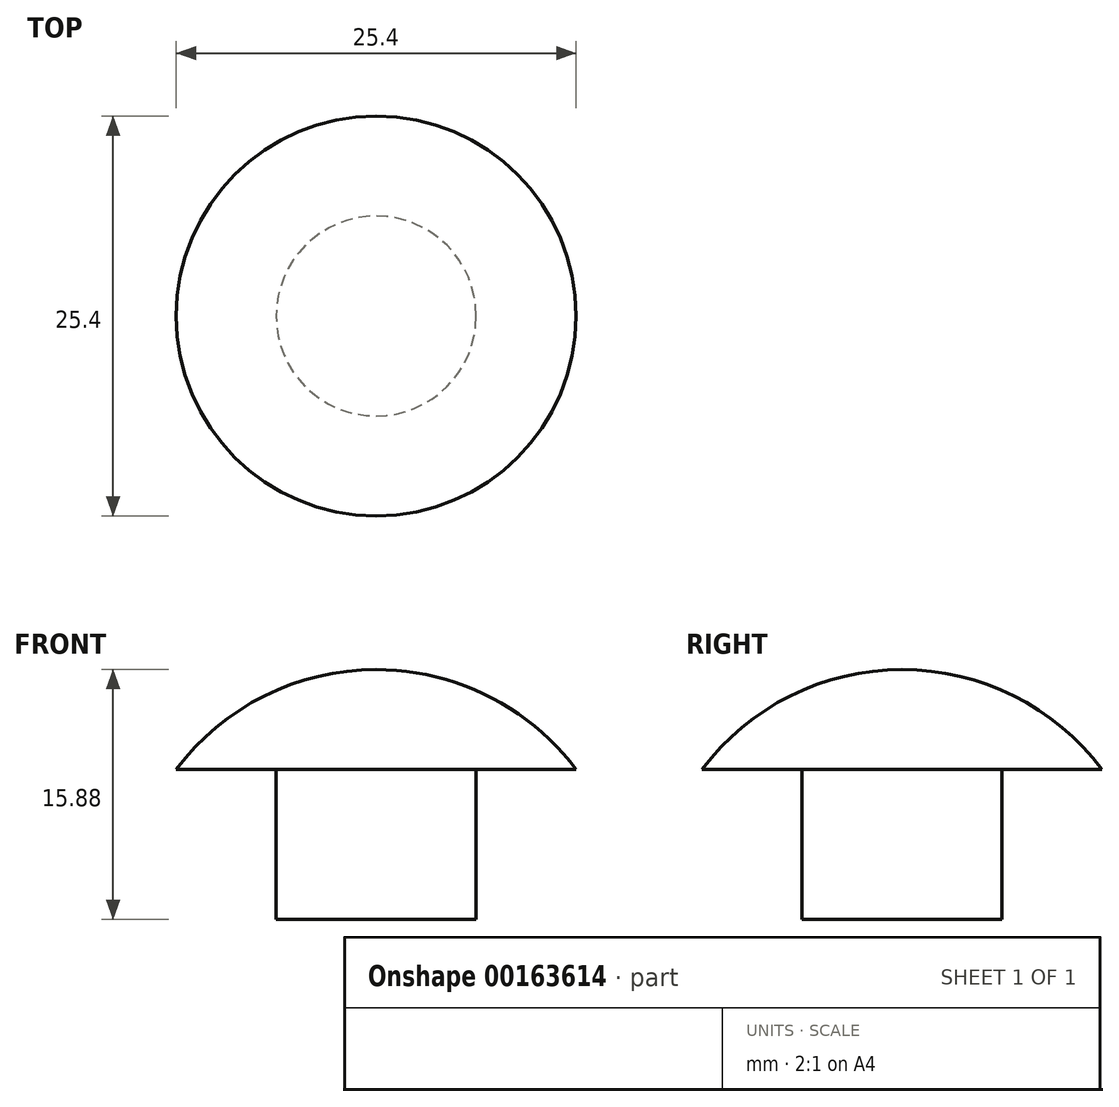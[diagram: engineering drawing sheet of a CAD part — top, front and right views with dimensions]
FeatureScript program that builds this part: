
annotation { "Feature Type Name" : "Feature", "Feature Type Description" : "" }
export const myFeature = defineFeature(function(context is Context, id is Id, definition is map)
    precondition{}
    {
        {
            var Q0;
            Q0=qCreatedBy(makeId("Front.planeOp"),FACE);
            var sketch = newSketch(context, id + "F0", { "sketchPlane" : qUnion([Q0])});
            skLineSegment(sketch, "E0", {"start": v(0, 0) * mm, "end": v(6.35, 0) * mm});
            skLineSegment(sketch, "E1", {"start": v(6.35, 0) * mm, "end": v(6.35, 9.53) * mm});
            skLineSegment(sketch, "E2", {"start": v(6.35, 9.53) * mm, "end": v(12.7, 9.53) * mm});
            skArc(sketch, "E3", {"start": v(12.7, 9.53) * mm, "mid": v(7.1, 14.2) * mm, "end": v(0, 15.88) * mm});
            skLineSegment(sketch, "E4", {"start": v(0, 15.88) * mm, "end": v(0, 0) * mm});
            skLineSegment(sketch, "E5", {"start": v(0, 57.47) * mm, "end": v(0, -64.96) * mm, "construction": true});
            skSolve(sketch);
        }
        {
            var Q0;
            Q0=makeQuery(id+"F0.imprint","IMPRINT",FACE,{"disambiguationData":[TD([[makeQuery(id+"F0.imprint","IMPRINT",EDGE,{"derivedFrom":sQuery(id+"F0.wireOp",EDGE,"E0")}),1.0]])]});
            var Q1;
            Q1=sQuery(id+"F0.wireOp",EDGE,"E5");
            revolve(context, id + "F1", {"entities" : qUnion([Q0]), "axis" : qUnion([Q1]), "revolveType" : RevolveType.FULL});
        }
    });
